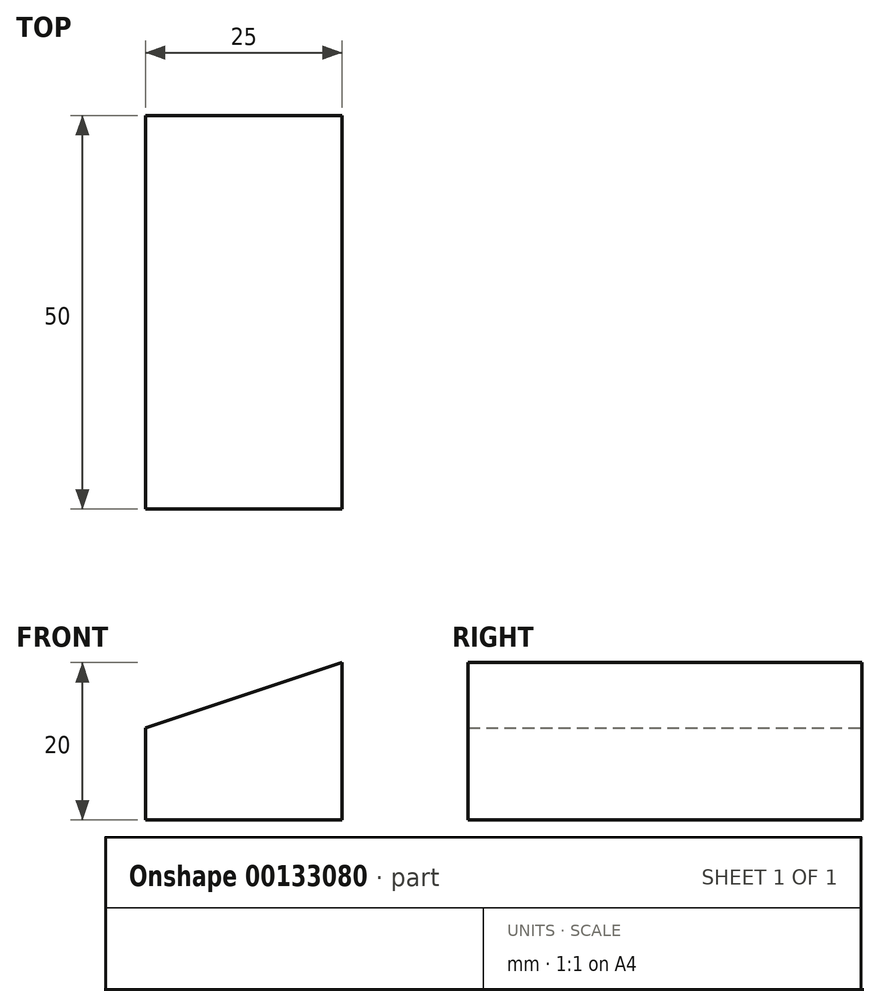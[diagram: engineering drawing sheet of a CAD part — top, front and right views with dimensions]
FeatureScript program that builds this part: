
annotation { "Feature Type Name" : "Feature", "Feature Type Description" : "" }
export const myFeature = defineFeature(function(context is Context, id is Id, definition is map)
    precondition{}
    {
        {
            var Q0;
            Q0=qCreatedBy(makeId("Front.planeOp"),FACE);
            var sketch = newSketch(context, id + "F0", { "sketchPlane" : qUnion([Q0])});
            skLineSegment(sketch, "E0.bottom", {"start": v(24.26, 22.62) * mm, "end": v(-25.74, 22.62) * mm});
            skLineSegment(sketch, "E0.top", {"start": v(24.26, -27.38) * mm, "end": v(-25.74, -27.38) * mm});
            skLineSegment(sketch, "E0.left", {"start": v(24.26, 22.62) * mm, "end": v(24.26, -27.38) * mm});
            skLineSegment(sketch, "E0.right", {"start": v(-25.74, 22.62) * mm, "end": v(-25.74, -27.38) * mm});
            skPoint(sketch, "E0.middle", {"position": v(-0.74, -2.38) * mm});
            skLineSegment(sketch, "E1", {"start": v(-25.74, -2.38) * mm, "end": v(-0.74, -2.38) * mm});
            skLineSegment(sketch, "E2", {"start": v(-25.74, 22.62) * mm, "end": v(-10.74, 22.62) * mm});
            skLineSegment(sketch, "E3", {"start": v(24.26, 22.62) * mm, "end": v(24.26, 7.62) * mm});
            skLineSegment(sketch, "E4", {"start": v(24.26, -27.38) * mm, "end": v(14.26, -27.38) * mm});
            skLineSegment(sketch, "E5", {"start": v(-10.74, 22.62) * mm, "end": v(-10.74, 7.62) * mm});
            skLineSegment(sketch, "E6", {"start": v(-10.74, 7.62) * mm, "end": v(-0.74, 7.62) * mm});
            skLineSegment(sketch, "E7", {"start": v(-0.74, 7.62) * mm, "end": v(-0.74, -2.38) * mm});
            skLineSegment(sketch, "E8", {"start": v(-25.74, -2.38) * mm, "end": v(-25.74, -12.38) * mm});
            skLineSegment(sketch, "E9", {"start": v(-0.74, -2.38) * mm, "end": v(-0.74, -17.38) * mm});
            skLineSegment(sketch, "E10", {"start": v(-0.74, -17.38) * mm, "end": v(-0.74, -2.38) * mm});
            skLineSegment(sketch, "E11", {"start": v(-0.74, -17.38) * mm, "end": v(-10.74, -17.38) * mm});
            skLineSegment(sketch, "E12", {"start": v(-10.74, -17.38) * mm, "end": v(-25.74, -12.38) * mm});
            skLineSegment(sketch, "E13", {"start": v(14.26, -27.38) * mm, "end": v(14.26, -17.38) * mm});
            skLineSegment(sketch, "E14", {"start": v(-0.74, -12.38) * mm, "end": v(6.76, -12.38) * mm});
            skLineSegment(sketch, "E15", {"start": v(6.76, -12.38) * mm, "end": v(6.76, -17.38) * mm});
            skLineSegment(sketch, "E16", {"start": v(6.76, -17.38) * mm, "end": v(14.26, -17.38) * mm});
            skLineSegment(sketch, "E17", {"start": v(-5.74, 7.62) * mm, "end": v(-0.74, 7.62) * mm});
            skLineSegment(sketch, "E18", {"start": v(-5.74, 12.62) * mm, "end": v(24.26, 22.62) * mm});
            skLineSegment(sketch, "E19", {"start": v(24.26, 7.62) * mm, "end": v(24.26, 2.62) * mm});
            skLineSegment(sketch, "E20", {"start": v(24.26, 2.62) * mm, "end": v(4.26, 2.62) * mm});
            skLineSegment(sketch, "E21", {"start": v(4.26, 2.62) * mm, "end": v(-0.74, -2.38) * mm});
            skPoint(sketch, "E22.endSnap0", {"position": v(-5.74, 10.12) * mm});
            skLineSegment(sketch, "E23", {"start": v(-5.74, 12.62) * mm, "end": v(-5.74, 10.12) * mm});
            skLineSegment(sketch, "E24", {"start": v(-5.74, 10.12) * mm, "end": v(-3.24, 10.12) * mm});
            skPoint(sketch, "E24.endSnap0", {"position": v(-3.24, 7.62) * mm});
            skLineSegment(sketch, "E25", {"start": v(-3.24, 10.12) * mm, "end": v(-0.74, 10.12) * mm});
            skLineSegment(sketch, "E26", {"start": v(-0.74, 10.12) * mm, "end": v(-0.74, 7.62) * mm});
            skLineSegment(sketch, "E27", {"start": v(-0.74, 7.62) * mm, "end": v(-0.74, 14.29) * mm});
            skLineSegment(sketch, "E28", {"start": v(4.26, 2.62) * mm, "end": v(-0.74, 2.62) * mm});
            skSolve(sketch);
        }
        {
            var Q0;
            Q0=makeQuery(id+"F0.imprint","IMPRINT",FACE,{"disambiguationData":[TD([[makeQuery(id+"F0.imprint","IMPRINT",EDGE,{"derivedFrom":sQuery(id+"F0.wireOp",EDGE,"E0.left")}),-1.0]])]});
            extrude(context, id + "F1", {"entities" : qUnion([Q0]), "depth" : 50 * mm});
        }
    });
